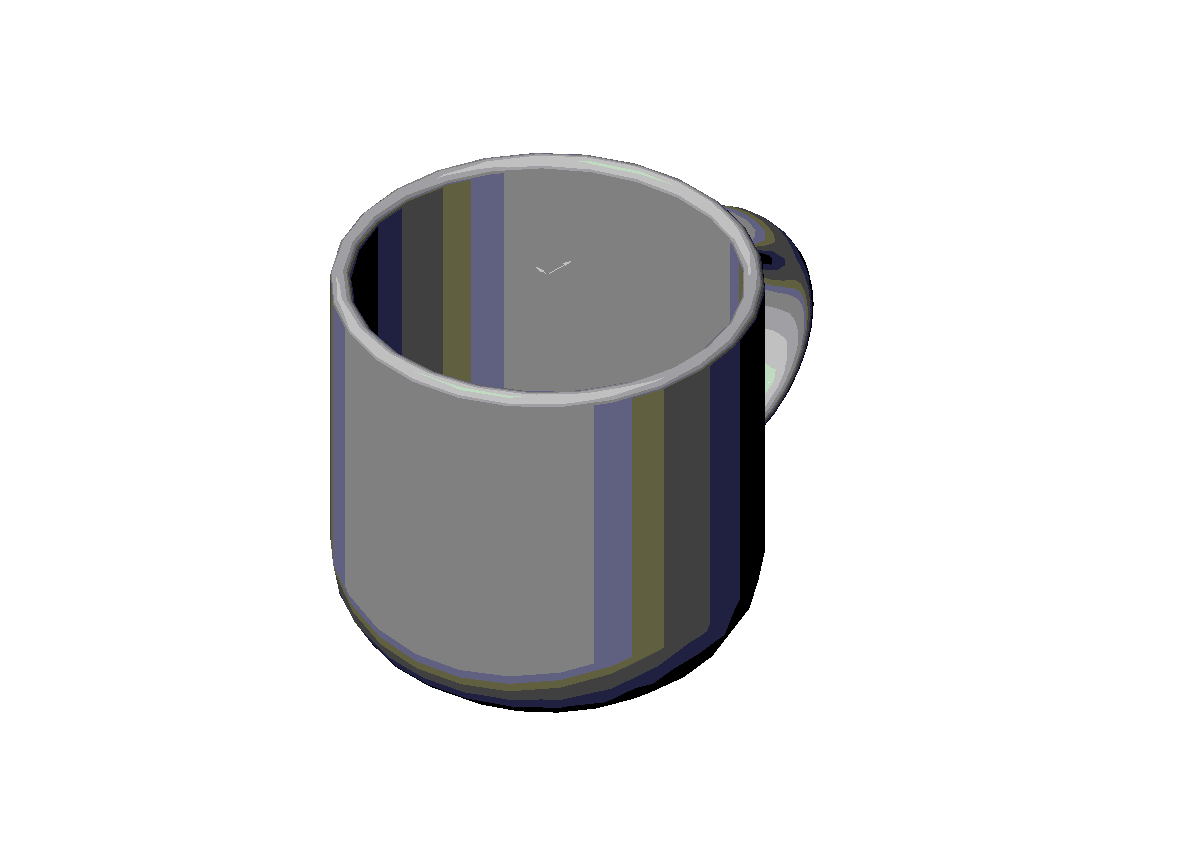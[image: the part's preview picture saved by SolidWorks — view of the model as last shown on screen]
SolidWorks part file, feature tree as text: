
SOLIDWORKS PART (.sldprt)
format: sldprt  version: not decoded by parser v0  size: 190,976 bytes
history: native  units: mm
features: plane x5, sketch x3, fillet x2, extrude x1, shell x1, sweep x1 (+5 scaffold rows collapsed)
feature tree (18):
  scaffold x5  (default folders/planes/origin — collapsed)
  plane  "Plane1"
  plane  "Plan2"
  plane  "Plane3"
  sketch  "Sketch1"
  extrude  "Base-Extrude"  Depth=200mm
  fillet  "Fillet1"  Radius=50mm
  shell  "Shell1"  Thickness=10mm
  plane  "Plane4"
  plane  "Plane5"  Offset=95mm
  sketch  "Sketch2"
  sketch  "Sketch3"  dims[D1=55.0mm]
  sweep  "Boss-Sweep1"
  fillet  "Fillet2"  Radius=5mm
decode coverage: 5 of 8 modeling features carry decoded parameters
note: suppression state not decoded; provenance and decode notes live in map.json
